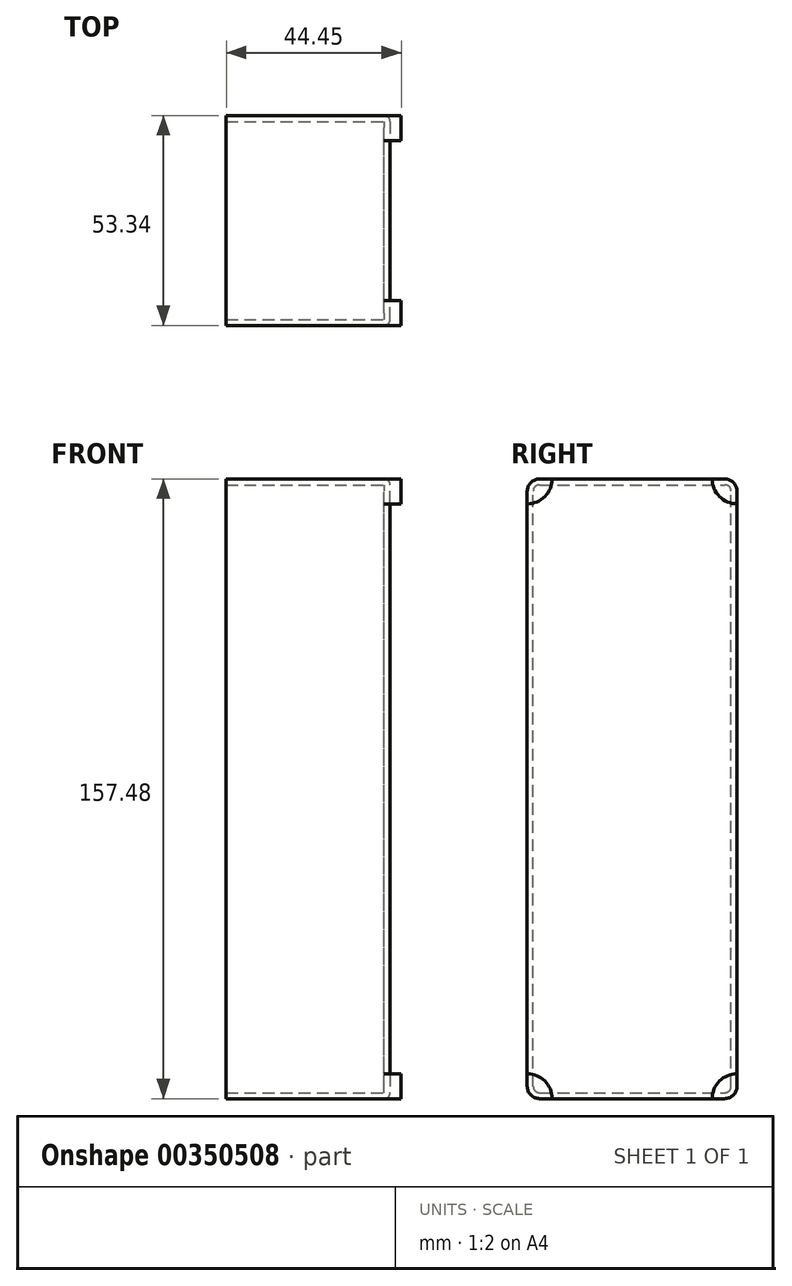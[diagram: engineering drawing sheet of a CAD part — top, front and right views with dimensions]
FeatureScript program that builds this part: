
annotation { "Feature Type Name" : "Feature", "Feature Type Description" : "" }
export const myFeature = defineFeature(function(context is Context, id is Id, definition is map)
    precondition{}
    {
        {
            var Q0;
            Q0=qCreatedBy(makeId("Right.planeOp"),FACE);
            var sketch = newSketch(context, id + "F0", { "sketchPlane" : qUnion([Q0])});
            skLineSegment(sketch, "E0.bottom", {"start": v(23.5, 78.74) * mm, "end": v(-23.5, 78.74) * mm});
            skLineSegment(sketch, "E0.top", {"start": v(23.5, -78.74) * mm, "end": v(-23.5, -78.74) * mm});
            skLineSegment(sketch, "E0.left", {"start": v(26.67, 75.57) * mm, "end": v(26.67, -75.57) * mm});
            skLineSegment(sketch, "E0.right", {"start": v(-26.67, 75.57) * mm, "end": v(-26.67, -75.57) * mm});
            skPoint(sketch, "E0.middle", {"position": v(0, 0) * mm});
            skPoint(sketch, "E1.visualSharp", {"position": v(-26.67, 78.74) * mm});
            skArc(sketch, "E1.filletArc", {"start": v(-23.5, 78.74) * mm, "mid": v(-25.74, 77.81) * mm, "end": v(-26.67, 75.57) * mm});
            skPoint(sketch, "E2.visualSharp", {"position": v(26.67, 78.74) * mm});
            skArc(sketch, "E2.filletArc", {"start": v(26.67, 75.57) * mm, "mid": v(25.74, 77.81) * mm, "end": v(23.5, 78.74) * mm});
            skPoint(sketch, "E3.visualSharp", {"position": v(26.67, -78.74) * mm});
            skArc(sketch, "E3.filletArc", {"start": v(23.5, -78.74) * mm, "mid": v(25.74, -77.81) * mm, "end": v(26.67, -75.57) * mm});
            skPoint(sketch, "E4.visualSharp", {"position": v(-26.67, -78.74) * mm});
            skArc(sketch, "E4.filletArc", {"start": v(-26.67, -75.57) * mm, "mid": v(-25.74, -77.81) * mm, "end": v(-23.5, -78.74) * mm});
            skSolve(sketch);
        }
        {
            var Q0;
            Q0=qSketchRegion(id+"F0",true);
            extrude(context, id + "F1", {"entities" : qUnion([Q0]), "depth" : 1.52 * mm});
        }
        {
            var Q0;
            Q0=makeQuery(id+"F1.opExtrude","CAP_FACE",FACE,{"disambiguationData":[OSD([sQuery(id+"F0.wireOp",EDGE,"E0.bottom"),sQuery(id+"F0.wireOp",EDGE,"E0.top"),sQuery(id+"F0.wireOp",EDGE,"E0.left"),sQuery(id+"F0.wireOp",EDGE,"E0.right"),sQuery(id+"F0.wireOp",EDGE,"E1.filletArc"),sQuery(id+"F0.wireOp",EDGE,"E2.filletArc"),sQuery(id+"F0.wireOp",EDGE,"E3.filletArc"),sQuery(id+"F0.wireOp",EDGE,"E4.filletArc")])],"isStart":true});
            var sketch = newSketch(context, id + "F2", { "sketchPlane" : qUnion([Q0])});
            skPoint(sketch, "E5.middle", {"position": v(0, 0) * mm});
            skLineSegment(sketch, "E6.bottom", {"start": v(23.56, -77.22) * mm, "end": v(-23.56, -77.22) * mm});
            skLineSegment(sketch, "E6.top", {"start": v(23.56, 77.22) * mm, "end": v(-23.56, 77.22) * mm});
            skLineSegment(sketch, "E6.left", {"start": v(25.15, -75.63) * mm, "end": v(25.15, 75.63) * mm});
            skLineSegment(sketch, "E6.right", {"start": v(-25.15, -75.63) * mm, "end": v(-25.15, 75.63) * mm});
            skPoint(sketch, "E7.visualSharp", {"position": v(25.15, 77.22) * mm});
            skArc(sketch, "E7.filletArc", {"start": v(25.15, 75.63) * mm, "mid": v(24.68, 76.75) * mm, "end": v(23.56, 77.22) * mm});
            skPoint(sketch, "E8.visualSharp", {"position": v(25.15, -77.22) * mm});
            skArc(sketch, "E8.filletArc", {"start": v(23.56, -77.22) * mm, "mid": v(24.68, -76.75) * mm, "end": v(25.15, -75.63) * mm});
            skPoint(sketch, "E9.visualSharp", {"position": v(-25.15, -77.22) * mm});
            skArc(sketch, "E9.filletArc", {"start": v(-25.15, -75.63) * mm, "mid": v(-24.68, -76.75) * mm, "end": v(-23.56, -77.22) * mm});
            skPoint(sketch, "E10.visualSharp", {"position": v(-25.15, 77.22) * mm});
            skArc(sketch, "E10.filletArc", {"start": v(-23.56, 77.22) * mm, "mid": v(-24.68, 76.75) * mm, "end": v(-25.15, 75.63) * mm});
            skSolve(sketch);
        }
        {
            var Q0;
            Q0=makeQuery(id+"F2.imprint","IMPRINT",FACE,{"disambiguationData":[TD([[makeQuery(id+"F2.imprint","IMPRINT",EDGE,{"derivedFrom":sQuery(id+"F2.wireOp",EDGE,"E6.bottom")}),1.0]])]});
            extrude(context, id + "F3", {"entities" : qUnion([Q0]), "operationType" : NewBodyOperationType.ADD, "depth" : 40.13 * mm});
        }
        {
            var Q0;
            Q0=makeQuery(id+"F1.opExtrude","CAP_FACE",FACE,{"disambiguationData":[OSD([sQuery(id+"F0.wireOp",EDGE,"E0.bottom"),sQuery(id+"F0.wireOp",EDGE,"E0.top"),sQuery(id+"F0.wireOp",EDGE,"E0.left"),sQuery(id+"F0.wireOp",EDGE,"E0.right"),sQuery(id+"F0.wireOp",EDGE,"E1.filletArc"),sQuery(id+"F0.wireOp",EDGE,"E2.filletArc"),sQuery(id+"F0.wireOp",EDGE,"E3.filletArc"),sQuery(id+"F0.wireOp",EDGE,"E4.filletArc")])],"isStart":false});
            var sketch = newSketch(context, id + "F4", { "sketchPlane" : qUnion([Q0])});
            skLineSegment(sketch, "E11", {"start": v(-11.46, 78.74) * mm, "end": v(-32.66, 78.74) * mm, "construction": true});
            skLineSegment(sketch, "E12", {"start": v(-26.67, 6.72) * mm, "end": v(-26.67, 24.4) * mm, "construction": true});
            skCircle(sketch, "E13", {"center": v(-26.67, 78.74) * mm, "radius": 6.35 * mm});
            skSolve(sketch);
        }
        {
            var Q0;
            {var subQ5=makeQuery(id+"F1.opExtrude","CAP_EDGE",EDGE,{"disambiguationData":[OSD([sQuery(id+"F0.wireOp",EDGE,"E1.filletArc")])],"isStart":false});Q0=makeQuery(id+"F4.imprint","IMPRINT",FACE,{"disambiguationData":[TD([[makeQuery(id+"F4.imprint","IMPRINT",EDGE,{"derivedFrom":subQ5}),1.0]])]});}
            extrude(context, id + "F5", {"entities" : qUnion([Q0]), "depth" : 2.8 * mm});
        }
        {
            var Q0;
            Q0=makeQuery(id+"F5.opExtrude","SWEPT_BODY",BODY,{"disambiguationData":[OSD([sQuery(id+"F0.wireOp",EDGE,"E0.bottom"),sQuery(id+"F0.wireOp",EDGE,"E0.right"),sQuery(id+"F0.wireOp",EDGE,"E1.filletArc"),sQuery(id+"F4.wireOp",EDGE,"E13")])]});
            var Q1;
            Q1=qCreatedBy(makeId("Top.planeOp"),FACE);
            mirror(context, id + "F6", {"entities" : qUnion([Q0]), "mirrorPlane" : qUnion([Q1])});
        }
        {
            var Q0;
            Q0=makeQuery(id+"F6.opPattern","COPY",BODY,{"derivedFrom":makeQuery(id+"F5.opExtrude","SWEPT_BODY",BODY,{"disambiguationData":[OSD([sQuery(id+"F0.wireOp",EDGE,"E0.bottom"),sQuery(id+"F0.wireOp",EDGE,"E0.right"),sQuery(id+"F0.wireOp",EDGE,"E1.filletArc"),sQuery(id+"F4.wireOp",EDGE,"E13")])]}),"instanceName":"1"});
            var Q1;
            Q1=makeQuery(id+"F5.opExtrude","SWEPT_BODY",BODY,{"disambiguationData":[OSD([sQuery(id+"F0.wireOp",EDGE,"E0.bottom"),sQuery(id+"F0.wireOp",EDGE,"E0.right"),sQuery(id+"F0.wireOp",EDGE,"E1.filletArc"),sQuery(id+"F4.wireOp",EDGE,"E13")])]});
            var Q2;
            Q2=qCreatedBy(makeId("Front.planeOp"),FACE);
            mirror(context, id + "F7", {"operationType" : NewBodyOperationType.ADD, "entities" : qUnion([Q0, Q1]), "mirrorPlane" : qUnion([Q2])});
        }
        {
            var Q0;
            Q0=makeQuery(id+"F1.opExtrude","CAP_EDGE",EDGE,{"disambiguationData":[OSD([sQuery(id+"F0.wireOp",EDGE,"E0.right")])],"isStart":false});
            fillet(context, id + "F8", {"entities" : qUnion([Q0]), "radius" : 1.59 * mm, "tangentPropagation" : true, "allowEdgeOverflow" : false});
        }
        {
            var Q0;
            Q0=makeQuery(id+"F1.opExtrude","CAP_EDGE",EDGE,{"disambiguationData":[OSD([sQuery(id+"F0.wireOp",EDGE,"E0.top")])],"isStart":false});
            fillet(context, id + "F9", {"entities" : qUnion([Q0]), "radius" : 1.59 * mm, "tangentPropagation" : true, "allowEdgeOverflow" : false});
        }
        {
            var Q0;
            Q0=makeQuery(id+"F1.opExtrude","CAP_EDGE",EDGE,{"disambiguationData":[OSD([sQuery(id+"F0.wireOp",EDGE,"E0.left")])],"isStart":false});
            fillet(context, id + "F10", {"entities" : qUnion([Q0]), "radius" : 1.59 * mm, "tangentPropagation" : true, "allowEdgeOverflow" : false});
        }
        {
            var Q0;
            Q0=makeQuery(id+"F1.opExtrude","CAP_EDGE",EDGE,{"disambiguationData":[OSD([sQuery(id+"F0.wireOp",EDGE,"E0.bottom")])],"isStart":false});
            fillet(context, id + "F11", {"entities" : qUnion([Q0]), "radius" : 1.59 * mm, "tangentPropagation" : true, "allowEdgeOverflow" : false});
        }
    });
